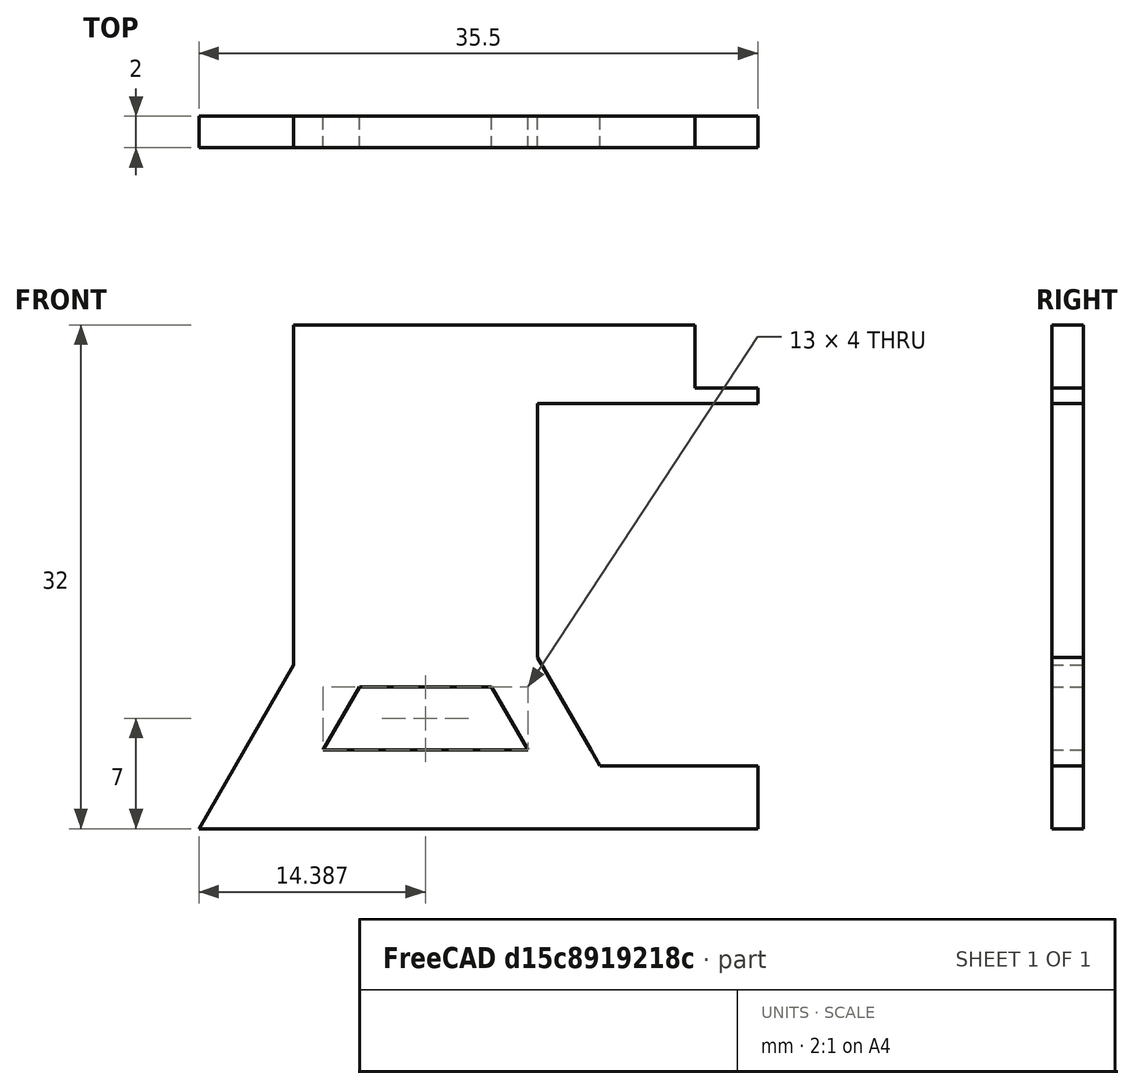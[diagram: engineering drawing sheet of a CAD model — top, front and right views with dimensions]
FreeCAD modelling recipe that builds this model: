
FCSTD DOCUMENT  (FreeCAD 0.14R3700 (Git))
Label: BIRR_fixMoteurPileAv
License: CC-BY 3.0
LicenseURL: http://creativecommons.org/licenses/by/3.0/
objects: Sketcher::SketchObject×1, Part::Extrusion×1, Part::Feature×1
note: 3 computed .brp shape members not serialized (recipe doc carries the construction recipe); baked Part::Feature solids carry a one-line shape summary decoded from their .brp

FEATURE [Sketcher::SketchObject] Sketch  label="fixMoteurPileAv"
  Placement = pos=(0,0,0) rot=(1,0,0;1.5708rad)
  sketch-geometry (18):
    g0: LineSegment StartX=-27.6132 StartY=-11 StartZ=0 EndX=-25.3038 EndY=-7 EndZ=0
    g1: LineSegment StartX=0 StartY=11 StartZ=0 EndX=-14 EndY=11 EndZ=0
    g2: LineSegment StartX=-25.3038 StartY=-7 StartZ=0 EndX=-16.9226 EndY=-7 EndZ=0
    g3: LineSegment StartX=-16.9226 StartY=-7 StartZ=0 EndX=-14.6132 EndY=-11 EndZ=0
    g4: LineSegment StartX=-29.5 StartY=16 StartZ=0 EndX=-4 EndY=16 EndZ=0
    g5: LineSegment StartX=0 StartY=-12 StartZ=0 EndX=0 EndY=-16 EndZ=0
    g6: LineSegment StartX=-29.5 StartY=16 StartZ=0 EndX=-29.5 EndY=-5.6077 EndZ=0
    g7: LineSegment StartX=-14 StartY=11 StartZ=0 EndX=-14 EndY=-5.13397 EndZ=0
    g8: LineSegment StartX=0 StartY=-12 StartZ=0 EndX=-10.0359 EndY=-12 EndZ=0
    g9: LineSegment StartX=-27.6132 StartY=-11 StartZ=0 EndX=-14.6132 EndY=-11 EndZ=0
    g10: LineSegment StartX=-35.5 StartY=-16 StartZ=0 EndX=-32.6132 EndY=-11 EndZ=0
    g11: LineSegment StartX=-32.6132 StartY=-11 StartZ=0 EndX=-29.5 EndY=-5.6077 EndZ=0
    g12: LineSegment StartX=0 StartY=-16 StartZ=0 EndX=-35.5 EndY=-16 EndZ=0
    g13: LineSegment StartX=0 StartY=11 StartZ=0 EndX=0 EndY=12 EndZ=0
    g14: LineSegment StartX=0 StartY=12 StartZ=0 EndX=-4 EndY=12 EndZ=0
    g15: LineSegment StartX=-4 StartY=12 StartZ=0 EndX=-4 EndY=16 EndZ=0
    g16: LineSegment StartX=-14 StartY=-5.13397 StartZ=0 EndX=-10.6132 EndY=-11 EndZ=0
    g17: LineSegment StartX=-10.6132 StartY=-11 StartZ=0 EndX=-10.0359 EndY=-12 EndZ=0
  constraints (54):
    c: Horizontal(g1)
    c: Coincident(g2,g0)
    c: Horizontal(g2)
    c: Coincident(g3,g2)
    c: PointOnObject(g1,g-2)
    c: Horizontal(g4)
    c: Vertical(g5)
    c: PointOnObject(g5,g-2)
    c: DistanceY(g1,g5) = -23
    c: DistanceY(g5) = -4
    c: Coincident(g6,g4)
    c: Vertical(g6)
    c: Coincident(g7,g1)
    c: Vertical(g7)
    c: Coincident(g8,g5)
    c: Horizontal(g8)
    c: DistanceY(g0,g0) = 4
    c: Coincident(g9,g0)
    c: Horizontal(g9)
    c: Coincident(g9,g3)
    c: Angle(g9,g0) = 1.0472
    c: Angle(g3,g9) = 1.0472
    c: Parallel(g10,g0)
    c: PointOnObject(g10,g9)
    c: Coincident(g11,g10)
    c: Coincident(g11,g6)
    c: Parallel(g0,g11)
    c: DistanceX(g10,g0) = 5
    c: DistanceX(g9) = 13
    c: Coincident(g12,g5)
    c: Coincident(g12,g10)
    c: Horizontal(g12)
    c: DistanceX(g12) = -35.5
    c: DistanceX(g1) = -14
    c: DistanceX(g4,g1) = 29.5
    c: DistanceY(g1,g4) = 5
    c: DistanceY(g-1,g5) = -16
    c: Coincident(g13,g1)
    c: Vertical(g13)
    c: Coincident(g14,g13)
    c: Horizontal(g14)
    c: Coincident(g15,g14)
    c: Coincident(g15,g4)
    c: Vertical(g15)
    c: DistanceX(g14) = -4
    c: DistanceY(g15) = 4
    c: DistanceY(g10,g0) = 5
    c: Coincident(g16,g7)
    c: Coincident(g17,g16)
    c: Coincident(g17,g8)
    c: Parallel(g16,g17)
    c: DistanceX(g3,g16) = 4
    c: PointOnObject(g16,g9)
    c: Parallel(g3,g16)
FEATURE [Part::Extrusion] Extrude
  Base = -> Sketch
  Dir = (0,2,0)
  Solid = true
FEATURE [Part::Feature] Extrude001  label="fixMoteurPileAv_copy"
  shape: bbox 35.5 x 2 x 32 mm, 20 faces (baked)
